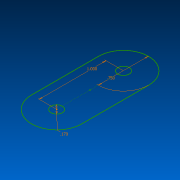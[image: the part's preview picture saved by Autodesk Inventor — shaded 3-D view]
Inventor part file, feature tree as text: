
AUTODESK INVENTOR PART (.ipt)
format: ipt  version: 2022.2 (Build 262287000, 287)  size: 71,168 bytes
history: native  units: in
note: dims shown in document units (in); Inventor stores cm internally (conversion verified against a paired STEP export)
features: sketch x1
ambient origin geometry x8: Origin, YZ Plane, XZ Plane, XY Plane, X Axis, Y Axis, Z Axis, Center Point
feature tree (1):
  sketch  "Sketch1"  dims[d0=0.17in d2=1.0in d3=0.75in]
